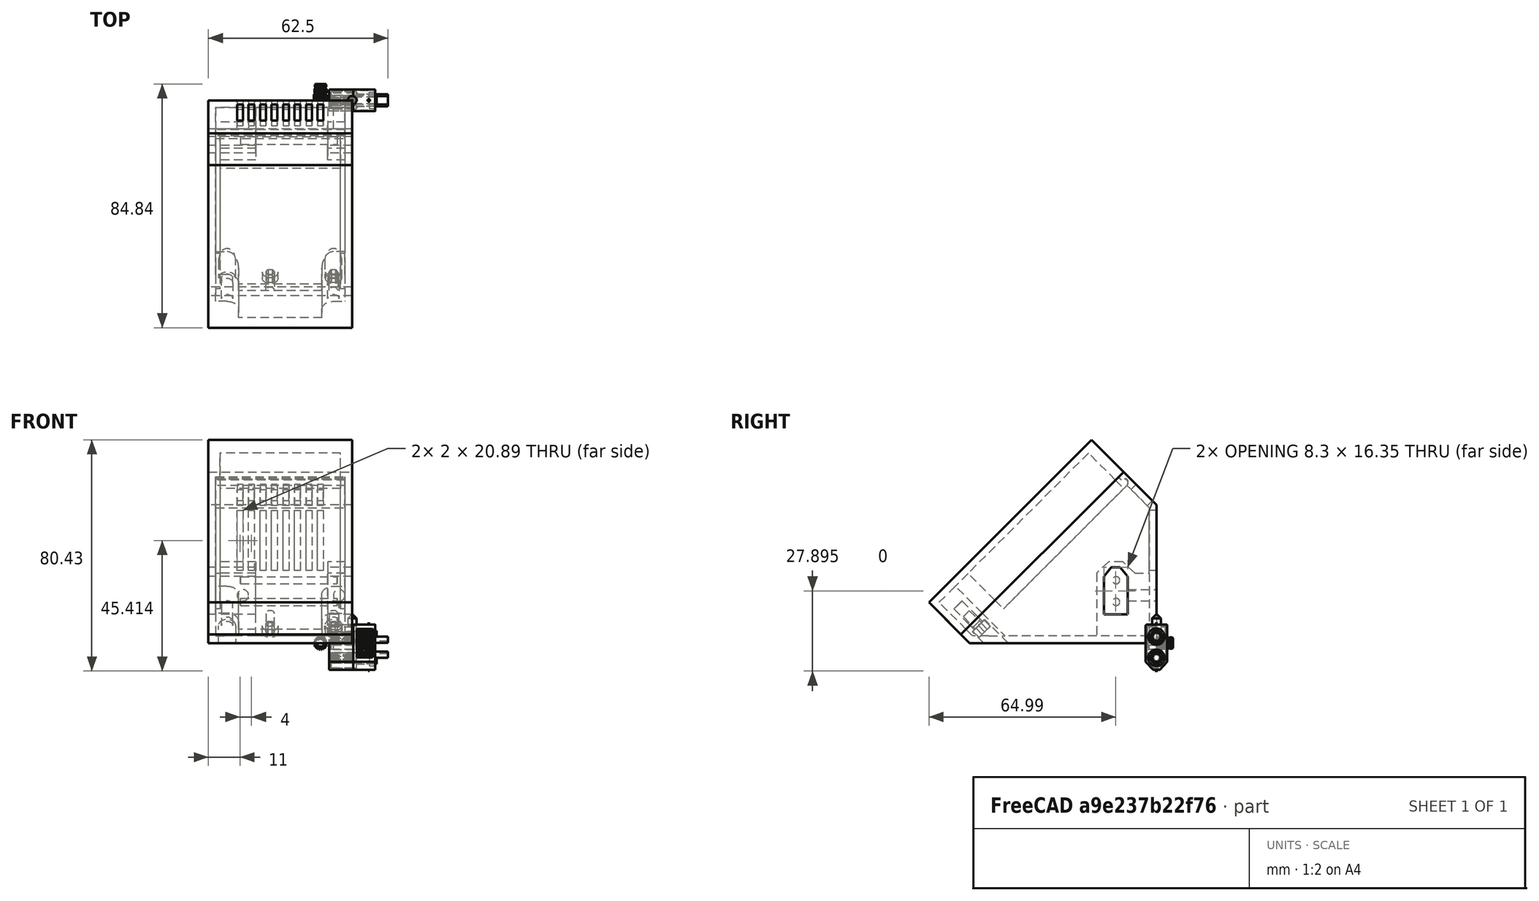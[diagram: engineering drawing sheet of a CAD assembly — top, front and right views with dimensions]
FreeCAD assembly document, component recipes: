
FREECAD ASSEMBLY — COMPONENT RECIPES ("base35mm_009.1")

This assembly document has 8 components, labeled P0..P7 below (a component is one placed body or linked part). 6 of them carry a construction recipe — the FreeCAD feature program that regenerates the part from scratch, quoted from this document or its linked companion documents; the rest are supplied as boundary geometry only. No exploded tour is included for this assembly.
COMPONENT P0 — recipe-attached ("base", modeled in this document).
Construction recipe (the document's own serialized feature program — sketch geometry with constraints, then the solid features built on it; lengths are millimeters unless a unit is written):

FEATURE [PartDesign::FeatureBase] Clone
  BaseFeature = -> Slice_child0
FEATURE [PartDesign::Thickness] Thickness
  Base = -> Clone [Face7]
  BaseFeature = -> Clone
  Intersection = false
  Join = 0
  Mode = 0
  Reversed = true
  SupportTransform = false
  Value = 2.5
  expr: Value = <<sp>>.epaisseurParois
FEATURE [PartDesign::Plane] DatumPlane001  label="planXt"
  AttachmentOffset = pos=(0,0,-2.5) rot=(0,0,1;0rad)
  Length = 110.737
  MapMode = 5
  Placement = pos=(-2.5,6e-16,-6e-16) rot=(0.57735,0.57735,0.57735;2.0944rad)
  ResizeMode = 0
  Support = -> [YZ_Plane002]
  Width = 102.305
  expr: .AttachmentOffset.Base.z = -<<sp>>.epaisseurParois
FEATURE [Sketcher::SketchObject] Sketch002  label="sk_renfortXt"
  FullyConstrained = true
  MapMode = 5
  Placement = pos=(-2.5,6e-16,-6e-16) rot=(0.57735,0.57735,0.57735;2.0944rad)
  Support = -> [DatumPlane001]
  expr: .Constraints.dist = <<sp>>.xt60distanceAngleBord
  expr: .Constraints.epRf = <<sp>>.xt60epRenfort
  expr: Constraints[13] = <<sp>>.xt60largeurFetiere
  expr: Constraints[14] = <<sp>>.xt60hauteur
  expr: Constraints[15] = <<sp>>.xt60hauteurToit
  expr: Constraints[16] = <<sp>>.xt60base
  expr: Constraints[18] = .Constraints.dist
  expr: Constraints[31] = <<sp>>.epaisseurParois
  expr: Constraints[32] = .Constraints.epRf
  expr: Constraints[34] = .Constraints.epRf
  expr: Constraints[45] = <<sp>>.epaisseurParois
  sketch-geometry (17):
    g0: LineSegment StartX=-18.3 StartY=10 StartZ=0 EndX=-18.3 EndY=23.25 EndZ=0
    g1: LineSegment StartX=-18.3 StartY=23.25 StartZ=0 EndX=-15.65 EndY=25.75 EndZ=0
    g2: LineSegment StartX=-15.65 StartY=25.75 StartZ=0 EndX=-12.65 EndY=25.75 EndZ=0
    g3: LineSegment StartX=-12.65 StartY=25.75 StartZ=0 EndX=-10 EndY=23.25 EndZ=0
    g4: LineSegment StartX=-10 StartY=23.25 StartZ=0 EndX=-10 EndY=10 EndZ=0
    g5: LineSegment StartX=-10 StartY=10 StartZ=0 EndX=-18.3 EndY=10 EndZ=0
    g6: LineSegment StartX=-14.15 StartY=10 StartZ=0 EndX=-14.15 EndY=25.75 EndZ=0
    g7: LineSegment StartX=-16.6431 StartY=28.25 StartZ=0 EndX=-20.8 EndY=24.3284 EndZ=0
    g8: LineSegment StartX=-20.8 StartY=24.3284 StartZ=0 EndX=-20.8 EndY=2.5 EndZ=0
    g9: LineSegment StartX=-20.8 StartY=2.5 StartZ=0 EndX=-7.5 EndY=2.5 EndZ=0
    g10: LineSegment StartX=-7.5 StartY=2.5 StartZ=0 EndX=-7.5 EndY=24.3284 EndZ=0
    g11: LineSegment StartX=-7.5 StartY=24.3284 StartZ=0 EndX=-11.6569 EndY=28.25 EndZ=0
    g12: LineSegment StartX=-11.6569 StartY=28.25 StartZ=0 EndX=-16.6431 EndY=28.25 EndZ=0
    g13: LineSegment StartX=-7.5 StartY=24.3284 StartZ=0 EndX=-2.5 EndY=24.3284 EndZ=0
    g14: LineSegment StartX=-2.5 StartY=24.3284 StartZ=0 EndX=-2.5 EndY=2.5 EndZ=0
    g15: LineSegment StartX=-2.5 StartY=2.5 StartZ=0 EndX=-7.5 EndY=2.5 EndZ=0
    g16: LineSegment StartX=-7.5 StartY=2.5 StartZ=0 EndX=-7.5 EndY=24.3284 EndZ=0
  constraints (46):
    c: Vertical(g0)
    c: Coincident(g0,g1)
    c: Coincident(g1,g2)
    c: Horizontal(g2)
    c: Coincident(g2,g3)
    c: Coincident(g3,g4)
    c: Vertical(g4)
    c: Coincident(g4,g5)
    c: Coincident(g5,g0)
    c: Horizontal(g5)
    c: Symmetric(g1,g2,g6)
    c: Equal(g0,g4)
    c: Symmetric(g0,g4,g6)
    c: DistanceX(g2,g2) = 3
    c: DistanceY(g4,g4) = 13.25
    c: DistanceY(g3,g2) = 2.5
    c: DistanceX(g5,g5) = 8.3
    c: DistanceX(g4,g-1) = 10  'dist'
    c: DistanceY(g-1,g4) = 10
    c: Coincident(g7,g8)
    c: Vertical(g8)
    c: Coincident(g8,g9)
    c: Horizontal(g9)
    c: Coincident(g9,g10)
    c: Coincident(g10,g11)
    c: Coincident(g11,g12)
    c: Coincident(g12,g7)
    c: Symmetric(g7,g10,g6)
    c: Symmetric(g7,g11,g6)
    c: Symmetric(g8,g9,g6)
    c: DistanceX(g8,g0) = 2.5  'epRf'
    c: DistanceY(g-1,g9) = 2.5
    c: Distance(g7,g1) = 2.5
    c: Parallel(g1,g7)
    c: DistanceY(g2,g11) = 2.5
    c: Coincident(g13,g14)
    c: Coincident(g14,g15)
    c: Coincident(g15,g16)
    c: Coincident(g16,g13)
    c: Horizontal(g13)
    c: Horizontal(g15)
    c: Vertical(g14)
    c: Vertical(g16)
    c: Coincident(g13,g11)
    c: Horizontal(g14,g9)
    c: DistanceX(g14,g-1) = 2.5
FEATURE [PartDesign::Pad] Pad001  label="renfortXt"
  AllowMultiFace = false
  BaseFeature = -> Thickness
  Direction = (1,-1e-16,1e-16)
  Length = 45
  Length2 = 100
  Profile = -> Sketch002
  Reversed = true
  Type = 0
  expr: Length = <<sp>>.largeurModuleBase - 2 * <<sp>>.epaisseurParois
FEATURE [Sketcher::SketchObject] Sketch003  label="sk_trouXt"
  FullyConstrained = true
  MapMode = 5
  Placement = pos=(0,0,0) rot=(0.57735,0.57735,0.57735;2.0944rad)
  Support = -> [YZ_Plane002]
  expr: .Constraints.dist = <<sp>>.xt60distanceAngleBord
  expr: Constraints[13] = <<sp>>.xt60base
  expr: Constraints[14] = <<sp>>.xt60hauteur
  expr: Constraints[15] = <<sp>>.xt60hauteurToit + <<sp>>.xtJeu
  expr: Constraints[16] = <<sp>>.xt60largeurFetiere
  expr: Constraints[18] = .Constraints.dist
  sketch-geometry (7):
    g0: LineSegment StartX=-18.3 StartY=10 StartZ=0 EndX=-18.3 EndY=23.25 EndZ=0
    g1: LineSegment StartX=-18.3 StartY=23.25 StartZ=0 EndX=-15.65 EndY=26.35 EndZ=0
    g2: LineSegment StartX=-15.65 StartY=26.35 StartZ=0 EndX=-12.65 EndY=26.35 EndZ=0
    g3: LineSegment StartX=-12.65 StartY=26.35 StartZ=0 EndX=-10 EndY=23.25 EndZ=0
    g4: LineSegment StartX=-10 StartY=23.25 StartZ=0 EndX=-10 EndY=10 EndZ=0
    g5: LineSegment StartX=-10 StartY=10 StartZ=0 EndX=-18.3 EndY=10 EndZ=0
    g6: LineSegment StartX=-14.15 StartY=10 StartZ=0 EndX=-14.15 EndY=26.35 EndZ=0
  constraints (19):
    c: Vertical(g0)
    c: Coincident(g0,g1)
    c: Coincident(g1,g2)
    c: Horizontal(g2)
    c: Coincident(g2,g3)
    c: Coincident(g3,g4)
    c: Coincident(g4,g5)
    c: Coincident(g5,g0)
    c: Horizontal(g5)
    c: Symmetric(g1,g2,g6)
    c: Symmetric(g0,g3,g6)
    c: Vertical(g6)
    c: Symmetric(g0,g4,g6)
    c: DistanceX(g5,g5) = 8.3
    c: DistanceY(g4,g4) = 13.25
    c: DistanceY(g3,g2) = 3.1
    c: DistanceX(g2,g2) = 3
    c: DistanceX(g4,g-1) = 10  'dist'
    c: DistanceY(g-1,g4) = 10
FEATURE [PartDesign::Pocket] Pocket
  AllowMultiFace = false
  BaseFeature = -> Pad001
  Direction = (-1,2e-16,-3e-16)
  Length = 50
  Length2 = 100
  Profile = -> Sketch003
  Type = 0
  expr: Length = <<sp>>.largeurModuleBase
FEATURE [PartDesign::Plane] DatumPlane002  label="planDecoupeRenfortXt"
  AttachmentOffset = pos=(0,0,2.5) rot=(0,0,1;0rad)
  Length = 90.9281
  MapMode = 5
  Placement = pos=(0,-2.5,-6e-16) rot=(1,0,0;1.5708rad)
  ResizeMode = 0
  Support = -> [XZ_Plane002]
  Width = 100.497
  expr: .AttachmentOffset.Base.z = <<sp>>.epaisseurParois
FEATURE [Sketcher::SketchObject] Sketch004  label="sk_decoupRenfXt"
  FullyConstrained = true
  MapMode = 5
  Placement = pos=(0,-2.5,-6e-16) rot=(1,0,0;1.5708rad)
  Support = -> [DatumPlane002]
  expr: Constraints[10] = <<sp>>.xt60LongueurRenfortPetit + <<sp>>.epaisseurParois
  expr: Constraints[11] = <<sp>>.largeurModuleBase - (<<sp>>.xt60longueurRenfortGrand + <<sp>>.epaisseurParois)
  expr: Constraints[8] = <<sp>>.epaisseurParois
  expr: Constraints[9] = <<sp>>.xt60distanceAngleBord + <<sp>>.xt60hauteur + <<sp>>.xt60hauteurToit + <<sp>>.xt60epRenfort
  sketch-geometry (4):
    g0: LineSegment StartX=-33.5 StartY=28.25 StartZ=0 EndX=-8.5 EndY=28.25 EndZ=0
    g1: LineSegment StartX=-8.5 StartY=28.25 StartZ=0 EndX=-8.5 EndY=2.5 EndZ=0
    g2: LineSegment StartX=-8.5 StartY=2.5 StartZ=0 EndX=-33.5 EndY=2.5 EndZ=0
    g3: LineSegment StartX=-33.5 StartY=2.5 StartZ=0 EndX=-33.5 EndY=28.25 EndZ=0
  constraints (12):
    c: Coincident(g0,g1)
    c: Coincident(g1,g2)
    c: Coincident(g2,g3)
    c: Coincident(g3,g0)
    c: Horizontal(g0)
    c: Horizontal(g2)
    c: Vertical(g1)
    c: Vertical(g3)
    c: DistanceY(g-1,g1) = 2.5
    c: DistanceY(g-1,g0) = 28.25
    c: DistanceX(g1,g-1) = 8.5
    c: DistanceX(g2,g-1) = 33.5
FEATURE [PartDesign::Pocket] Pocket001  label="decoupeRenfXt"
  AllowMultiFace = false
  BaseFeature = -> Pocket
  Direction = (0,1,2e-16)
  Length = 23.3
  Length2 = 100
  Profile = -> Sketch004
  Reversed = true
  Type = 0
  expr: Length = <<sp>>.xt60distanceAngleBord + <<sp>>.xt60base + 2 * <<sp>>.xt60epRenfort
FEATURE [Sketcher::SketchObject] Sketch005  label="xt60PercagePostMale"
  FullyConstrained = true
  MapMode = 5
  Placement = pos=(0,0,0) rot=(1,0,0;1.5708rad)
  Support = -> [XZ_Plane002]
  expr: Constraints[0] = <<sp>>.insertDiamPercage
  expr: Constraints[1] = <<sp>>.insertDistanceTrouBordMale
  expr: Constraints[2] = <<sp>>.insertHauteur
  sketch-geometry (1):
    g0: Circle CenterX=-4.5 CenterY=16.625 CenterZ=0 NormalX=0 NormalY=0 NormalZ=1 AngleXU=0 Radius=2
  constraints (3):
    c: Diameter(g0) = 4
    c: DistanceX(g0,g-1) = 4.5
    c: DistanceY(g-1,g0) = 16.625
FEATURE [PartDesign::Pocket] Pocket002  label="insertXtMale"
  AllowMultiFace = false
  BaseFeature = -> Pocket001
  Direction = (0,1,2e-16)
  Length = 10
  Length2 = 100
  Profile = -> Sketch005
  Reversed = true
  Type = 0
  expr: Length = <<sp>>.insertProfondeurPercage
FEATURE [Sketcher::SketchObject] Sketch006  label="xt60PercagePostFem"
  FullyConstrained = true
  MapMode = 5
  Placement = pos=(0,0,0) rot=(1,0,0;1.5708rad)
  Support = -> [XZ_Plane002]
  expr: Constraints[0] = <<sp>>.insertDiamPercage
  expr: Constraints[1] = <<sp>>.insertDistanceTrouBordFem
  expr: Constraints[2] = <<sp>>.insertHauteur
  sketch-geometry (1):
    g0: Circle CenterX=-38 CenterY=16.625 CenterZ=0 NormalX=0 NormalY=0 NormalZ=1 AngleXU=0 Radius=2
  constraints (3):
    c: Diameter(g0) = 4
    c: DistanceX(g0,g-1) = 38
    c: DistanceY(g-1,g0) = 16.625
FEATURE [PartDesign::Pocket] Pocket003  label="insertXt60Fem"
  AllowMultiFace = false
  BaseFeature = -> Pocket002
  Direction = (0,1,2e-16)
  Length = 10
  Length2 = 100
  Profile = -> Sketch006
  Reversed = true
  Type = 0
  expr: Length = <<sp>>.insertProfondeurPercage
FEATURE [PartDesign::Plane] DatumPlane003
  AttachmentOffset = pos=(0,0,2.5) rot=(0,0,1;0rad)
  Length = 91.7033
  MapMode = 2
  Placement = pos=(0,0,2.5) rot=(0,0,1;0rad)
  ResizeMode = 0
  Support = -> [XY_Plane002]
  Width = 109.703
  expr: .AttachmentOffset.Base.z = <<sp>>.epaisseurParois
FEATURE [PartDesign::Plane] DatumPlane004  label="planTrancheur"
  AttachmentOffset = pos=(0,0,71) rot=(-1,0,0;0.785398rad)
  Length = 94.4082
  MapMode = 5
  Placement = pos=(0,-71,-1.58e-14) rot=(1,0,0;0.785398rad)
  ResizeMode = 0
  Support = -> [XZ_Plane002]
  Width = 144.968
  expr: .AttachmentOffset.Base.z = <<sp>>.planTrancheur
FEATURE [Sketcher::SketchObject] Sketch008
  FullyConstrained = true
  MapMode = 5
  Placement = pos=(0,-71,-2.13e-14) rot=(1,0,0;0.785398rad)
  Support = -> [DatumPlane004]
  expr: .Constraints.dist = <<sp>>.epaisseurParois
  expr: Constraints[13] = <<sp>>.epaisseurParois
  expr: Constraints[16] = <<sp>>.insertDiamPercage / 2 + <<sp>>.insertFAVMargeDist
  expr: Constraints[1] = <<sp>>.insertFavDistAuZeroDuPLan
  expr: Constraints[21] = <<sp>>.insertFAVDistBord
  expr: Constraints[22] = <<sp>>.largeurModuleBase - <<sp>>.epaisseurParois
  sketch-geometry (7):
    g0: LineSegment StartX=-2.5 StartY=4.24264 StartZ=0 EndX=-47.5 EndY=4.24264 EndZ=0
    g1: LineSegment StartX=-6.5 StartY=14.7426 StartZ=0 EndX=-2.5 EndY=14.7426 EndZ=0
    g2: LineSegment StartX=-2.5 StartY=14.7426 StartZ=0 EndX=-2.5 EndY=6.74264 EndZ=0
    g3: LineSegment StartX=-2.5 StartY=6.74264 StartZ=0 EndX=-10.5 EndY=6.74264 EndZ=0
    g4: LineSegment StartX=-10.5 StartY=6.74264 StartZ=0 EndX=-10.5 EndY=10.7426 EndZ=0
    g5: ArcOfCircle CenterX=-6.5 CenterY=10.7426 CenterZ=0 NormalX=0 NormalY=0 NormalZ=1 AngleXU=0 Radius=4 StartAngle=1.5708 EndAngle=3.14159
    g6: LineSegment StartX=-6.5 StartY=10.7426 StartZ=0 EndX=-6.5 EndY=6.74264 EndZ=0
  constraints (23):
    c: Horizontal(g0)
    c: DistanceY(g-1,g0) = 4.24264
    c: DistanceX(g0,g-1) = 2.5  'dist'
    c: Horizontal(g1)
    c: Coincident(g1,g2)
    c: Vertical(g2)
    c: Coincident(g2,g3)
    c: Horizontal(g3)
    c: Coincident(g3,g4)
    c: Vertical(g4)
    c: Vertical(g2,g0)
    c: Equal(g3,g2)
    c: Equal(g4,g1)
    c: DistanceY(g0,g2) = 2.5
    c: Coincident(g5,g4)
    c: Coincident(g5,g1)
    c: DistanceX(g5,g2) = 4
    c: Coincident(g6,g5)
    c: PointOnObject(g6,g3)
    c: Vertical(g6)
    c: Vertical(g5,g1)
    c: DistanceX(g3,g3) = 8
    c: DistanceX(g0,g-1) = 47.5
FEATURE [PartDesign::Pad] Pad003  label="padTrouFAVDroite"
  AllowMultiFace = false
  BaseFeature = -> Pocket003
  Direction = (0,-0.707107,0.707107)
  Length = 10
  Length2 = 100
  Profile = -> Sketch008
  Reversed = true
  Type = 3
  UpToFace = -> DatumPlane003
FEATURE [Sketcher::SketchObject] Sketch009
  FullyConstrained = true
  MapMode = 5
  Placement = pos=(0,-71,-2.13e-14) rot=(1,0,0;0.785398rad)
  Support = -> [DatumPlane004]
  expr: .Constraints.larg = <<sp>>.insertFAVDistBord
  expr: Constraints[11] = .Constraints.larg / 2
  expr: Constraints[12] = <<sp>>.largeurModuleBase
  expr: Constraints[13] = <<sp>>.insertFavDistAuZeroDuPLan
  expr: Constraints[14] = <<sp>>.epaisseurParois
  expr: Constraints[15] = <<sp>>.epaisseurParois
  expr: Constraints[8] = .Constraints.larg
  sketch-geometry (6):
    g0: LineSegment StartX=-47.5 StartY=6.74264 StartZ=0 EndX=-39.5 EndY=6.74264 EndZ=0
    g1: LineSegment StartX=-39.5 StartY=6.74264 StartZ=0 EndX=-39.5 EndY=10.7426 EndZ=0
    g2: LineSegment StartX=-43.5 StartY=14.7426 StartZ=0 EndX=-47.5 EndY=14.7426 EndZ=0
    g3: LineSegment StartX=-47.5 StartY=14.7426 StartZ=0 EndX=-47.5 EndY=6.74264 EndZ=0
    g4: ArcOfCircle CenterX=-43.5 CenterY=10.7426 CenterZ=0 NormalX=0 NormalY=0 NormalZ=1 AngleXU=0 Radius=4 StartAngle=0 EndAngle=1.5708
    g5: GeomPoint X=-50 Y=4.24264 Z=0
  constraints (16):
    c: Coincident(g0,g1)
    c: Coincident(g2,g3)
    c: Coincident(g3,g0)
    c: Horizontal(g0)
    c: Horizontal(g2)
    c: Vertical(g1)
    c: Vertical(g3)
    c: DistanceX(g0,g0) = 8  'larg'
    c: DistanceY(g3,g3) = 8
    c: Tangent(g2,g4) = -1.5708
    c: Tangent(g1,g4) = -1.5708
    c: DistanceX(g0,g4) = 4
    c: DistanceX(g5,g-1) = 50
    c: DistanceY(g-1,g5) = 4.24264
    c: DistanceX(g5,g0) = 2.5
    c: DistanceY(g5,g0) = 2.5
FEATURE [PartDesign::Pad] Pad004  label="padTrouFavGauche"
  AllowMultiFace = false
  BaseFeature = -> Pad003
  Direction = (0,-0.707107,0.707107)
  Length = 10
  Length2 = 100
  Profile = -> Sketch009
  Type = 3
  UpToFace = -> DatumPlane003 [Plane]
FEATURE [Sketcher::SketchObject] Sketch010
  FullyConstrained = true
  MapMode = 5
  Placement = pos=(0,-71,-2.13e-14) rot=(1,0,0;0.785398rad)
  Support = -> [DatumPlane004]
  expr: Constraints[0] = <<sp>>.insertFAVDistBord / 2 + <<sp>>.epaisseurParois
  expr: Constraints[1] = <<sp>>.insertFavDistAuZeroDuPLan + <<sp>>.epaisseurParois + <<sp>>.insertFAVDistBord / 2
  expr: Constraints[2] = <<sp>>.insertDiamPercage
  sketch-geometry (1):
    g0: Circle CenterX=-6.5 CenterY=10.7426 CenterZ=0 NormalX=0 NormalY=0 NormalZ=1 AngleXU=0 Radius=2
  constraints (3):
    c: DistanceX(g0,g-1) = 6.5
    c: DistanceY(g-1,g0) = 10.7426
    c: Diameter(g0) = 4
FEATURE [PartDesign::Pocket] Pocket004  label="trouDroit"
  AllowMultiFace = false
  BaseFeature = -> Pad004
  Direction = (0,0.707107,-0.707107)
  Length = 5
  Length2 = 100
  Profile = -> Sketch010
  Type = 1
FEATURE [Sketcher::SketchObject] Sketch011
  FullyConstrained = true
  MapMode = 5
  Placement = pos=(0,-71,-2.13e-14) rot=(1,0,0;0.785398rad)
  Support = -> [DatumPlane004]
  expr: Constraints[0] = <<sp>>.insertDiamPercage
  expr: Constraints[1] = <<sp>>.largeurModuleBase - <<sp>>.epaisseurParois - <<sp>>.insertFAVDistBord / 2
  expr: Constraints[2] = <<sp>>.insertFavDistAuZeroDuPLan + <<sp>>.epaisseurParois + <<sp>>.insertFAVDistBord / 2
  sketch-geometry (1):
    g0: Circle CenterX=-43.5 CenterY=10.7426 CenterZ=0 NormalX=0 NormalY=0 NormalZ=1 AngleXU=0 Radius=2
  constraints (3):
    c: Diameter(g0) = 4
    c: DistanceX(g0,g-1) = 43.5
    c: DistanceY(g-1,g0) = 10.7426
FEATURE [PartDesign::Pocket] Pocket005  label="trouGauche"
  AllowMultiFace = false
  BaseFeature = -> Pocket004
  Direction = (0,0.707107,-0.707107)
  Length = 5
  Length2 = 100
  Profile = -> Sketch011
  Type = 1
FEATURE [PartDesign::Plane] DatumPlane005  label="planTeteVisFav"
  AttachmentOffset = pos=(0,0,68) rot=(-1,0,0;0.785398rad)
  Length = 94.4082
  MapMode = 5
  Placement = pos=(0,-68,-1.51e-14) rot=(1,0,0;0.785398rad)
  ResizeMode = 0
  Support = -> [XZ_Plane002]
  Width = 144.968
  expr: .AttachmentOffset.Base.z = <<sp>>.planTrancheur - 3
FEATURE [Sketcher::SketchObject] Sketch012
  ExternalGeometry = -> [Pocket005]
  FullyConstrained = true
  MapMode = 5
  Placement = pos=(0,-68,-1.42e-14) rot=(1,0,0;0.785398rad)
  Support = -> [DatumPlane005]
  expr: Constraints[1] = <<sp>>.visM3DiamEncastrement
  sketch-geometry (2):
    g0: Circle CenterX=-6.5 CenterY=8.62132 CenterZ=0 NormalX=0 NormalY=0 NormalZ=1 AngleXU=0 Radius=3
    g1: Circle CenterX=-43.5 CenterY=8.62132 CenterZ=0 NormalX=0 NormalY=0 NormalZ=1 AngleXU=0 Radius=3
  constraints (4):
    c: Equal(g0,g1)
    c: Diameter(g1) = 6
    c: Coincident(g1,g-4)
    c: Coincident(g-3,g0)
FEATURE [PartDesign::Pocket] Pocket006  label="evidementTeteVisFav"
  AllowMultiFace = false
  BaseFeature = -> Pocket005
  Direction = (0,0.707107,-0.707107)
  Length = 20
  Length2 = 100
  Profile = -> Sketch012
  Type = 1
FEATURE [Sketcher::SketchObject] Sketch014
  FullyConstrained = true
  MapMode = 5
  Placement = pos=(0,0,0) rot=(1,0,0;1.5708rad)
  Support = -> [XZ_Plane002]
  expr: Constraints[12] = <<sp>>.xt60distanceAngleBord + <<sp>>.xt60hauteur + <<sp>>.ventilDistBordFente
  expr: Constraints[13] = <<sp>>.ventilLargeurFentes
  expr: Constraints[14] = <<sp>>.ventilEcartfente / 2
  expr: Constraints[15] = <<sp>>.hauteurDuDos - <<sp>>.ventilDistBordFente
  expr: Constraints[2] = <<sp>>.hauteurDuDos
  expr: Constraints[3] = <<sp>>.largeurModuleBase / 2
  sketch-geometry (5):
    g0: LineSegment StartX=-25 StartY=0 StartZ=0 EndX=-25 EndY=48.1371 EndZ=0
    g1: LineSegment StartX=-28 StartY=46.1371 StartZ=0 EndX=-26 EndY=46.1371 EndZ=0
    g2: LineSegment StartX=-26 StartY=46.1371 StartZ=0 EndX=-26 EndY=25.25 EndZ=0
    g3: LineSegment StartX=-26 StartY=25.25 StartZ=0 EndX=-28 EndY=25.25 EndZ=0
    g4: LineSegment StartX=-28 StartY=25.25 StartZ=0 EndX=-28 EndY=46.1371 EndZ=0
  constraints (16):
    c: PointOnObject(g0,g-1)
    c: Vertical(g0)
    c: DistanceY(g0,g0) = 48.1371
    c: DistanceX(g0,g-1) = 25
    c: Coincident(g1,g2)
    c: Coincident(g2,g3)
    c: Coincident(g3,g4)
    c: Coincident(g4,g1)
    c: Horizontal(g1)
    c: Horizontal(g3)
    c: Vertical(g2)
    c: Vertical(g4)
    c: DistanceY(g-1,g2) = 25.25
    c: DistanceX(g1,g1) = 2
    c: DistanceX(g2,g0) = 1
    c: DistanceY(g-1,g1) = 46.1371
FEATURE [PartDesign::Pocket] Pocket008  label="ventilFente1"
  AllowMultiFace = false
  BaseFeature = -> Pocket006
  Direction = (0,1,2e-16)
  Length = 2.5
  Length2 = 100
  Profile = -> Sketch014
  Reversed = true
  Type = 0
  expr: Length = <<sp>>.epaisseurParois
FEATURE [PartDesign::LinearPattern] LinearPattern  label="ventilDosRepeat1"
  BaseFeature = -> Pocket008
  Direction = -> Sketch014 [H_Axis]
  Length = 12
  Occurrences = 4
  Originals = -> [Pocket008]
  Reversed = true
  expr: Length = <<sp>>.ventilLargeurRepet
  expr: Occurrences = <<sp>>.ventilNbrFents
FEATURE [PartDesign::LinearPattern] LinearPattern001  label="ventilDosRepeat2"
  BaseFeature = -> LinearPattern
  Direction = -> Sketch014 [H_Axis]
  Length = 16
  Occurrences = 5
  Originals = -> [Pocket008]
  expr: Length = <<sp>>.ventilLargeurRepet + <<sp>>.ventilEcartfente + <<sp>>.ventilLargeurFentes
  expr: Occurrences = <<sp>>.ventilNbrFents + 1
FEATURE [PartDesign::Plane] DatumPlane006  label="planVentilSup"
  AttachmentOffset = pos=(0,0,-48.1371) rot=(1,0,0;0.785398rad)
  Length = 94.4082
  MapMode = 5
  Placement = pos=(0,48.1371,1.07e-14) rot=(1,0,0;2.35619rad)
  ResizeMode = 0
  Support = -> [XZ_Plane002]
  Width = 144.968
  expr: .AttachmentOffset.Base.z = -<<sp>>.hauteurDuDos
FEATURE [Sketcher::SketchObject] Sketch015
  FullyConstrained = true
  MapMode = 5
  Placement = pos=(0,48.1371,1.07e-14) rot=(1,0,0;2.35619rad)
  Support = -> [DatumPlane006]
  expr: Constraints[10] = <<sp>>.ventilLargeurFentes
  expr: Constraints[11] = (<<sp>>.largeurModuleBase + <<sp>>.ventilEcartfente) / 2
  expr: Constraints[8] = <<sp>>.distanceAuZeroPlanBorArriere + <<sp>>.ventilDistBordFente
  expr: Constraints[9] = <<sp>>.longPetitRetSupSansFav - 2 * <<sp>>.ventilDistBordFente - <<sp>>.favBordureProf
  sketch-geometry (4):
    g0: LineSegment StartX=-26 StartY=78.0926 StartZ=0 EndX=-28 EndY=78.0926 EndZ=0
    g1: LineSegment StartX=-28 StartY=78.0926 StartZ=0 EndX=-28 EndY=70.0761 EndZ=0
    g2: LineSegment StartX=-28 StartY=70.0761 StartZ=0 EndX=-26 EndY=70.0761 EndZ=0
    g3: LineSegment StartX=-26 StartY=70.0761 StartZ=0 EndX=-26 EndY=78.0926 EndZ=0
  constraints (12):
    c: Coincident(g0,g1)
    c: Coincident(g1,g2)
    c: Coincident(g2,g3)
    c: Coincident(g3,g0)
    c: Horizontal(g0)
    c: Horizontal(g2)
    c: Vertical(g1)
    c: Vertical(g3)
    c: DistanceY(g-1,g2) = 70.0761
    c: DistanceY(g2,g0) = 8.01652
    c: DistanceX(g0,g0) = 2
    c: DistanceX(g2,g-1) = 26
FEATURE [PartDesign::Pocket] Pocket009  label="ventilSupFente"
  AllowMultiFace = false
  BaseFeature = -> LinearPattern001
  Direction = (0,0.707107,0.707107)
  Length = 5
  Length2 = 100
  Profile = -> Sketch015
  Reversed = true
  Type = 0
FEATURE [PartDesign::LinearPattern] LinearPattern002  label="ventilSupRepeat1"
  BaseFeature = -> Pocket009
  Direction = -> Sketch015 [H_Axis]
  Length = 12
  Occurrences = 4
  Originals = -> [Pocket009]
  Reversed = true
  expr: Length = <<sp>>.ventilLargeurRepet
  expr: Occurrences = <<sp>>.ventilNbrFents
FEATURE [PartDesign::LinearPattern] LinearPattern003  label="ventilSupRepeat2"
  BaseFeature = -> LinearPattern002
  Direction = -> Sketch015 [H_Axis]
  Length = 16
  Occurrences = 5
  Originals = -> [Pocket009]
  expr: Length = <<sp>>.ventilLargeurRepet + <<sp>>.ventilEcartfente + <<sp>>.ventilLargeurFentes
  expr: Occurrences = <<sp>>.ventilNbrFents + 1
FEATURE [PartDesign::Body] Body001  label="base"
  BaseFeature = -> Slice_child0
  Group = -> [Clone,Thickness,DatumPlane001,Sketch002,Pad001,Sketch003,Pocket,DatumPlane002,Sketch004,Pocket001,Sketch005,Pocket002,Sketch006,Pocket003,DatumPlane003,DatumPlane004,Sketch008,Pad003,Sketch009,Pad004,Sketch010,Pocket004,Sketch011,Pocket005,DatumPlane005,Sketch012,Pocket006,Sketch014,Pocket008,LinearPattern,LinearPattern001,DatumPlane006,Sketch015,Pocket009,LinearPattern002,LinearPattern003,+3 more]
  Origin = -> Origin002
  Tip = -> Pocket015
COMPONENT P1 — recipe-attached ("faceAvant", modeled in this document).
Construction recipe (the document's own serialized feature program — sketch geometry with constraints, then the solid features built on it; lengths are millimeters unless a unit is written):

FEATURE [PartDesign::FeatureBase] Clone001
  BaseFeature = -> Slice_child1
FEATURE [PartDesign::Thickness] Thickness001
  Base = -> Clone001 [Face5]
  BaseFeature = -> Clone001
  Intersection = false
  Join = 0
  Mode = 0
  Reversed = true
  SupportTransform = false
  Value = 2.5
  expr: Value = <<sp>>.epaisseurParois
FEATURE [PartDesign::Plane] DatumPlane007  label="planTrancheurBis"
  AttachmentOffset = pos=(0,0,71) rot=(-1,0,0;0.785398rad)
  Length = 95.5901
  MapMode = 5
  Placement = pos=(0,-71,-1.58e-14) rot=(1,0,0;0.785398rad)
  ResizeMode = 0
  Support = -> [XZ_Plane003]
  Width = 161.907
  expr: .AttachmentOffset.Base.z = <<sp>>.planTrancheur
FEATURE [Sketcher::SketchObject] Sketch016  label="sk_insertFavDroit"
  FullyConstrained = true
  MapMode = 5
  Placement = pos=(0,-71,-2.13e-14) rot=(1,0,0;0.785398rad)
  Support = -> [DatumPlane007]
  expr: Constraints[11] = <<sp>>.insertFAVDistBord
  expr: Constraints[14] = <<sp>>.insertFAVDistBord / 2
  expr: Constraints[7] = <<sp>>.epaisseurParois
  expr: Constraints[8] = <<sp>>.insertFavDistAuZeroDuPLan + <<sp>>.epaisseurParois
  expr: Constraints[9] = <<sp>>.insertFAVDistBord
  sketch-geometry (5):
    g0: LineSegment StartX=-6.5 StartY=14.7426 StartZ=0 EndX=-2.5 EndY=14.7426 EndZ=0
    g1: LineSegment StartX=-2.5 StartY=14.7426 StartZ=0 EndX=-2.5 EndY=6.74264 EndZ=0
    g2: LineSegment StartX=-2.5 StartY=6.74264 StartZ=0 EndX=-10.5 EndY=6.74264 EndZ=0
    g3: LineSegment StartX=-10.5 StartY=6.74264 StartZ=0 EndX=-10.5 EndY=10.7426 EndZ=0
    g4: ArcOfCircle CenterX=-6.5 CenterY=10.7426 CenterZ=0 NormalX=0 NormalY=0 NormalZ=1 AngleXU=0 Radius=4 StartAngle=1.5708 EndAngle=3.14159
  constraints (15):
    c: Horizontal(g0)
    c: Coincident(g0,g1)
    c: Vertical(g1)
    c: Coincident(g1,g2)
    c: Horizontal(g2)
    c: Coincident(g2,g3)
    c: Vertical(g3)
    c: DistanceX(g1,g-1) = 2.5
    c: DistanceY(g-1,g1) = 6.74264
    c: DistanceY(g1,g1) = 8
    c: Equal(g3,g0)
    c: DistanceX(g2,g2) = 8
    c: Coincident(g4,g0)
    c: Tangent(g4,g3) = 1.5708
    c: DistanceX(g4,g1) = 4
FEATURE [PartDesign::Pad] Pad005  label="padInsertFavDroit"
  AllowMultiFace = false
  BaseFeature = -> Thickness001
  Direction = (0,-0.707107,0.707107)
  Length = 10
  Length2 = 100
  Profile = -> Sketch016
  Type = 2
FEATURE [Sketcher::SketchObject] Sketch017  label="sp_padInserFavGauch"
  FullyConstrained = true
  MapMode = 5
  Placement = pos=(0,-71,-2.13e-14) rot=(1,0,0;0.785398rad)
  Support = -> [DatumPlane007]
  expr: Constraints[10] = <<sp>>.insertFAVDistBord
  expr: Constraints[12] = <<sp>>.insertFAVDistBord / 2
  expr: Constraints[13] = <<sp>>.largeurModuleBase
  expr: Constraints[14] = <<sp>>.insertFavDistAuZeroDuPLan
  expr: Constraints[15] = <<sp>>.epaisseurParois
  expr: Constraints[16] = <<sp>>.epaisseurParois
  sketch-geometry (6):
    g0: LineSegment StartX=-43.5 StartY=14.7426 StartZ=0 EndX=-47.5 EndY=14.7426 EndZ=0
    g1: LineSegment StartX=-47.5 StartY=14.7426 StartZ=0 EndX=-47.5 EndY=6.74264 EndZ=0
    g2: LineSegment StartX=-47.5 StartY=6.74264 StartZ=0 EndX=-39.5 EndY=6.74264 EndZ=0
    g3: LineSegment StartX=-39.5 StartY=6.74264 StartZ=0 EndX=-39.5 EndY=10.7426 EndZ=0
    g4: ArcOfCircle CenterX=-43.5 CenterY=10.7426 CenterZ=0 NormalX=0 NormalY=0 NormalZ=1 AngleXU=0 Radius=4 StartAngle=0 EndAngle=1.5708
    g5: GeomPoint X=-50 Y=4.24264 Z=0
  constraints (17):
    c: Horizontal(g0)
    c: Coincident(g0,g1)
    c: Vertical(g1)
    c: Coincident(g1,g2)
    c: Horizontal(g2)
    c: Coincident(g2,g3)
    c: Vertical(g3)
    c: Equal(g3,g0)
    c: Equal(g2,g1)
    c: Coincident(g0,g4)
    c: DistanceX(g2,g2) = 8
    c: Tangent(g4,g3) = -1.5708
    c: DistanceX(g0,g0) = 4
    c: DistanceX(g5,g-1) = 50
    c: DistanceY(g-1,g5) = 4.24264
    c: DistanceY(g5,g1) = 2.5
    c: DistanceX(g5,g1) = 2.5
FEATURE [PartDesign::Pad] Pad006  label="padInsertFavGauch"
  AllowMultiFace = false
  BaseFeature = -> Pad005
  Direction = (0,-0.707107,0.707107)
  Length = 10
  Length2 = 100
  Profile = -> Sketch017
  Type = 2
FEATURE [Sketcher::SketchObject] Sketch018  label="skPercageInsertFavDroit"
  FullyConstrained = true
  MapMode = 5
  Placement = pos=(0,-71,-2.13e-14) rot=(1,0,0;0.785398rad)
  Support = -> [DatumPlane007]
  expr: Constraints[0] = <<sp>>.insertDiamPercage
  expr: Constraints[1] = <<sp>>.insertFavDistAuZeroDuPLan + <<sp>>.epaisseurParois + <<sp>>.insertFAVDistBord / 2
  expr: Constraints[2] = <<sp>>.epaisseurParois + <<sp>>.insertFAVDistBord / 2
  expr: Constraints[7] = <<sp>>.largeurModuleBase - 2 * <<sp>>.epaisseurParois - <<sp>>.insertFAVDistBord
  sketch-geometry (3):
    g0: Circle CenterX=-6.5 CenterY=10.7426 CenterZ=0 NormalX=0 NormalY=0 NormalZ=1 AngleXU=0 Radius=2
    g1: Circle CenterX=-43.5 CenterY=10.7426 CenterZ=0 NormalX=0 NormalY=0 NormalZ=1 AngleXU=0 Radius=2
    g2: LineSegment StartX=-43.5 StartY=10.7426 StartZ=0 EndX=-6.5 EndY=10.7426 EndZ=0
  constraints (8):
    c: Diameter(g0) = 4
    c: DistanceY(g-1,g0) = 10.7426
    c: DistanceX(g0,g-1) = 6.5
    c: Equal(g0,g1)
    c: Coincident(g2,g1)
    c: Coincident(g2,g0)
    c: Horizontal(g2)
    c: DistanceX(g2,g2) = 37
FEATURE [PartDesign::Pocket] Pocket010  label="trouInsertFavDroit"
  AllowMultiFace = false
  BaseFeature = -> Pad006
  Direction = (0,0.707107,-0.707107)
  Length = 8
  Length2 = 100
  Profile = -> Sketch018
  Reversed = true
  Type = 0
  expr: Length = <<sp>>.insertFavProfondeur
FEATURE [PartDesign::Plane] DatumPlane011  label="planFaceAvant"
  AttachmentOffset = pos=(0,0,93.2843) rot=(-1,0,0;0.785398rad)
  Length = 95.5901
  MapMode = 5
  Placement = pos=(0,-93.2843,-2.07e-14) rot=(1,0,0;0.785398rad)
  ResizeMode = 0
  Support = -> [XZ_Plane003]
  Width = 161.907
  expr: .AttachmentOffset.Base.z = <<sp>>.planFaceAvant
FEATURE [Sketcher::SketchObject] Sketch030  label="sk_rebordFav"
  FullyConstrained = true
  MapMode = 5
  Placement = pos=(0,-71,-2.13e-14) rot=(1,0,0;0.785398rad)
  Support = -> [DatumPlane007]
  expr: Constraints[0] = <<sp>>.insertFavDistAuZeroDuPLan
  expr: Constraints[19] = <<sp>>.epaisseurParois
  expr: Constraints[20] = <<sp>>.favEpBordure
  expr: Constraints[21] = <<sp>>.favDistBordPlan
  expr: Constraints[22] = <<sp>>.largeurModuleBase - 2 * <<sp>>.epaisseurParois
  expr: Constraints[23] = <<sp>>.favEpBordure
  expr: Constraints[24] = <<sp>>.Face - <<sp>>.epaisseurParois
  expr: Constraints[25] = <<sp>>.favEpBordure
  sketch-geometry (9):
    g0: GeomPoint X=0 Y=4.24264 Z=0
    g1: LineSegment StartX=-47.5 StartY=20.9853 StartZ=0 EndX=-47.5 EndY=81.7426 EndZ=0
    g2: LineSegment StartX=-47.5 StartY=81.7426 StartZ=0 EndX=-2.5 EndY=81.7426 EndZ=0
    g3: LineSegment StartX=-2.5 StartY=81.7426 StartZ=0 EndX=-2.5 EndY=20.9853 EndZ=0
    g4: LineSegment StartX=-2.5 StartY=20.9853 StartZ=0 EndX=-4 EndY=20.9853 EndZ=0
    g5: LineSegment StartX=-4 StartY=20.9853 StartZ=0 EndX=-4 EndY=80.2426 EndZ=0
    g6: LineSegment StartX=-4 StartY=80.2426 StartZ=0 EndX=-46 EndY=80.2426 EndZ=0
    g7: LineSegment StartX=-46 StartY=80.2426 StartZ=0 EndX=-46 EndY=20.9853 EndZ=0
    g8: LineSegment StartX=-46 StartY=20.9853 StartZ=0 EndX=-47.5 EndY=20.9853 EndZ=0
  constraints (26):
    c: DistanceY(g-1,g0) = 4.24264
    c: Vertical(g0,g-1)
    c: Vertical(g1)
    c: Coincident(g1,g2)
    c: Horizontal(g2)
    c: Coincident(g2,g3)
    c: Vertical(g3)
    c: Coincident(g3,g4)
    c: Horizontal(g4)
    c: Coincident(g4,g5)
    c: Vertical(g5)
    c: Coincident(g5,g6)
    c: Horizontal(g6)
    c: Coincident(g6,g7)
    c: Vertical(g7)
    c: Coincident(g7,g8)
    c: Coincident(g8,g1)
    c: Horizontal(g8)
    c: Horizontal(g7,g4)
    c: DistanceX(g3,g0) = 2.5
    c: DistanceX(g4,g4) = 1.5
    c: DistanceY(g0,g3) = 16.7426
    c: DistanceX(g1,g3) = 45
    c: DistanceY(g5,g2) = 1.5
    c: DistanceY(g0,g2) = 77.5
    c: DistanceX(g1,g7) = 1.5
FEATURE [PartDesign::Pad] Pad014  label="favRebordSupport"
  AllowMultiFace = false
  BaseFeature = -> Pocket010
  Direction = (0,-0.707107,0.707107)
  Length = 10
  Length2 = 100
  Profile = -> Sketch030
  Type = 3
  UpToFace = -> Pocket010 [Face13]
FEATURE [PartDesign::Pad] Pad015  label="favRebord"
  AllowMultiFace = false
  BaseFeature = -> Pad014
  Direction = (0,-0.707107,0.707107)
  Length = 4.15
  Length2 = 100
  Profile = -> Sketch030
  Reversed = true
  Type = 0
  expr: Length = <<sp>>.favBordureProf
FEATURE [Sketcher::SketchObject] Sketch031  label="sk_bourlet"
  ExternalGeometry = -> [Pad015]
  FullyConstrained = true
  MapMode = 5
  Placement = pos=(-2.5,0,0) rot=(0.57735,0.57735,0.57735;2.0944rad)
  Support = -> [Pad015]
  expr: Constraints[3] = <<sp>>.bourletMaintientRayon - <<sp>>.bourletRayonJeu
  sketch-geometry (2):
    g0: ArcOfCircle CenterX=-11.184 CenterY=55.7855 CenterZ=0 NormalX=0 NormalY=0 NormalZ=1 AngleXU=0 Radius=1.3 StartAngle=5.49779 EndAngle=8.63938
    g1: LineSegment StartX=-12.1032 StartY=56.7048 StartZ=0 EndX=-10.2647 EndY=54.8663 EndZ=0
  constraints (6):
    c: Coincident(g0,g-3)
    c: PointOnObject(g0,g-3)
    c: PointOnObject(g0,g-3)
    c: Radius(g0) = 1.3
    c: Coincident(g1,g0)
    c: Coincident(g1,g0)
FEATURE [PartDesign::Pad] Pad016  label="bourlet"
  AllowMultiFace = false
  BaseFeature = -> Pad015
  Direction = (1,0,0)
  Length = 10
  Length2 = 100
  Profile = -> Sketch031
  Reversed = true
  Type = 3
  UpToFace = -> Pad015 [Face11]
FEATURE [PartDesign::Body] Body002  label="faceAvant"
  BaseFeature = -> Slice_child1
  Group = -> [Clone001,Thickness001,DatumPlane007,Sketch016,Pad005,Sketch017,Pad006,Sketch018,Pocket010,DatumPlane011,Sketch030,Pad014,Pad015,Sketch031,Pad016]
  Origin = -> Origin003
  Tip = -> Pad016
COMPONENT P2 — recipe-attached ("Link", modeled in this document).
Construction recipe (the document's own serialized feature program — sketch geometry with constraints, then the solid features built on it; lengths are millimeters unless a unit is written):

FEATURE [Sketcher::SketchObject] Sketch  label="profileDeBase"
  FullyConstrained = true
  MapMode = 5
  Placement = pos=(0,0,0) rot=(0.57735,0.57735,0.57735;2.0944rad)
  Support = -> [YZ_Plane001]
  expr: Constraints[10] = <<sp>>.petitRetour
  expr: Constraints[11] = <<sp>>.angleFacePetitRetour
  expr: Constraints[12] = <<sp>>.Face
  expr: Constraints[13] = <<sp>>.angleFaceRetourHaut
  expr: Constraints[8] = <<sp>>.Base
  expr: Constraints[9] = <<sp>>.anglePetitRetourBase
  sketch-geometry (5):
    g0: LineSegment StartX=0 StartY=0 StartZ=0 EndX=-65 EndY=0 EndZ=0
    g1: LineSegment StartX=-65 StartY=0 StartZ=0 EndX=-79.1421 EndY=14.1421 EndZ=0
    g2: LineSegment StartX=-79.1421 StartY=14.1421 StartZ=0 EndX=-22.5736 EndY=70.7107 EndZ=0
    g3: LineSegment StartX=-22.5736 StartY=70.7107 StartZ=0 EndX=0 EndY=48.1371 EndZ=0
    g4: LineSegment StartX=0 StartY=48.1371 StartZ=0 EndX=0 EndY=0 EndZ=0
  constraints (14):
    c: Coincident(g-1,g0)
    c: Horizontal(g0)
    c: Coincident(g0,g1)
    c: Coincident(g1,g2)
    c: Coincident(g2,g3)
    c: PointOnObject(g3,g-2)
    c: Coincident(g3,g4)
    c: Coincident(g4,g0)
    c: DistanceX(g0,g0) = 65
    c: Angle(g0,g1) = 2.35619
    c: Distance(g1) = 20
    c: Angle(g1,g2) = 1.5708
    c: Distance(g2) = 80
    c: Angle(g2,g3) = 1.5708
FEATURE [PartDesign::Pad] Pad
  AllowMultiFace = false
  Direction = (1,-2e-16,3e-16)
  Length = 50
  Length2 = 100
  Placement = pos=(0,0,0) rot=(0.57735,0.57735,0.57735;2.0944rad)
  Profile = -> Sketch
  Reversed = true
  Type = 0
  expr: Length = <<sp>>.largeurModuleBase
FEATURE [PartDesign::Plane] DatumPlane
  AttachmentOffset = pos=(71,0,0) rot=(0,-1,0;0.785398rad)
  Length = 98.6412
  MapMode = 5
  Placement = pos=(-1.18e-14,1.18e-14,71) rot=(0.678598,0.678598,0.281085;3.68962rad)
  ResizeMode = 0
  Support = -> [Pad]
  Width = 63.0813
FEATURE [PartDesign::Body] Body  label="Base"
  Group = -> [Sketch,Pad,DatumPlane]
  Origin = -> Origin001
  Tip = -> Pad
COMPONENT P3 — recipe-attached ("tigeLaiton001", modeled in this document).
Construction recipe (the document's own serialized feature program — sketch geometry with constraints, then the solid features built on it; lengths are millimeters unless a unit is written):

FEATURE [PartDesign::Plane] DatumPlane012  label="planBaseTige"
  AttachmentOffset = pos=(0,0,-5.18) rot=(0,0,1;0rad)
  Length = 60
  MapMode = 5
  Placement = pos=(-5.18,1.2e-15,-1.2e-15) rot=(0.57735,0.57735,0.57735;2.0944rad)
  ResizeMode = 0
  Support = -> [YZ_Plane012]
  Width = 60
  expr: .AttachmentOffset.Base.z = -<<tige>>.planBaseTigeposX
FEATURE [Sketcher::SketchObject] Sketch032  label="sk_tiges"
  FullyConstrained = true
  MapMode = 5
  Placement = pos=(-5.18,1.2e-15,-1.2e-15) rot=(0.57735,0.57735,0.57735;2.0944rad)
  Support = -> [DatumPlane012]
  expr: Constraints[0] = <<tige>>.tigeDiam
  expr: Constraints[1] = <<tige>>.tigePosY
  expr: Constraints[2] = <<tige>>.tigePosX
  sketch-geometry (1):
    g0: Circle CenterX=-14 CenterY=14.3 CenterZ=0 NormalX=0 NormalY=0 NormalZ=1 AngleXU=0 Radius=1.25
  constraints (3):
    c: Diameter(g0) = 2.5
    c: DistanceY(g-1,g0) = 14.3
    c: DistanceX(g0,g-1) = 14
FEATURE [PartDesign::Pad] Pad017  label="tigeBasse"
  AllowMultiFace = false
  Direction = (1,-1e-16,1e-16)
  Length = 33.62
  Length2 = 100
  Placement = pos=(-5.18,1.2e-15,-1.2e-15) rot=(0.57735,0.57735,0.57735;2.0944rad)
  Profile = -> Sketch032
  Reversed = true
  Type = 0
  expr: Length = <<tige>>.tigeLong
FEATURE [PartDesign::Body] Body007  label="tigeLaiton"
  Group = -> [DatumPlane012,Sketch032,Pad017]
  Origin = -> Origin016
  Tip = -> Pad017
FEATURE [PartDesign::Plane] DatumPlane013  label="planTige2"
  AttachmentOffset = pos=(0,0,-5.18) rot=(0,0,1;0rad)
  Length = 60
  MapMode = 5
  Placement = pos=(-5.18,1.2e-15,-1.2e-15) rot=(0.57735,0.57735,0.57735;2.0944rad)
  ResizeMode = 0
  Support = -> [YZ_Plane014]
  Width = 60
  expr: .AttachmentOffset.Base.z = -<<tige>>.planBaseTigeposX
FEATURE [Sketcher::SketchObject] Sketch033  label="sk_tige2"
  FullyConstrained = true
  MapMode = 5
  Placement = pos=(-5.18,1.2e-15,-1.2e-15) rot=(0.57735,0.57735,0.57735;2.0944rad)
  Support = -> [DatumPlane013]
  expr: Constraints[0] = <<tige>>.tigeDiam
  expr: Constraints[1] = <<tige>>.tigePosX
  expr: Constraints[2] = <<tige>>.tigePosY + <<tige>>.xtEcartBroches
  sketch-geometry (1):
    g0: Circle CenterX=-14 CenterY=21.86 CenterZ=0 NormalX=0 NormalY=0 NormalZ=1 AngleXU=0 Radius=1.25
  constraints (3):
    c: Diameter(g0) = 2.5
    c: DistanceX(g0,g-1) = 14
    c: DistanceY(g-1,g0) = 21.86
FEATURE [PartDesign::Pad] Pad018
  AllowMultiFace = false
  Direction = (1,-1e-16,1e-16)
  Length = 33.62
  Length2 = 100
  Placement = pos=(-5.18,1.2e-15,-1.2e-15) rot=(0.57735,0.57735,0.57735;2.0944rad)
  Profile = -> Sketch033
  Reversed = true
  Type = 0
  expr: Length = <<tige>>.tigeLong
FEATURE [PartDesign::Body] Body008  label="tige2"
  Group = -> [DatumPlane013,Sketch033,Pad018]
  Origin = -> Origin018
  Tip = -> Pad018
COMPONENT P4 — geometry summary ("xtVisInsertFix"; no construction recipe available for this part):
  bounding box: 20.2 x 17.7 x 16.6 mm
  tessellated surface: 23,208 triangles
  volume: 1306 mm^3 (22% of its bounding box)
COMPONENT P5 — geometry summary ("xtVisInertMob"; no construction recipe available for this part):
  bounding box: 20.5 x 17.8 x 16.5 mm
  tessellated surface: 35,220 triangles
  volume: 1060 mm^3 (18% of its bounding box)
COMPONENT P6 — recipe-attached ("visInsertFavFix", modeled in this document).
Construction recipe (the document's own serialized feature program — sketch geometry with constraints, then the solid features built on it; lengths are millimeters unless a unit is written):

FEATURE [Sketcher::SketchObject] Sketch034  label="Sketch"
  FullyConstrained = false
  MapMode = 5
  Support = -> [XY_Plane015]
  sketch-geometry (1):
    g0: Circle CenterX=0 CenterY=0 CenterZ=0 NormalX=0 NormalY=0 NormalZ=1 AngleXU=0 Radius=2.75
  constraints (2):
    c: Coincident(g0,g-1)
    c: Diameter(g0) = 5.5
FEATURE [PartDesign::Pad] Pad019  label="tete"
  AllowMultiFace = false
  Direction = (1,1,1)
  Length = 3
  Length2 = 100
  Profile = -> Sketch034
  Type = 0
FEATURE [Sketcher::SketchObject] Sketch001
  FullyConstrained = false
  MapMode = 5
  Placement = pos=(0,0,0) rot=(1,0,0;3.14159rad)
  Support = -> [Pad019]
  sketch-geometry (1):
    g0: Circle CenterX=0 CenterY=0 CenterZ=0 NormalX=0 NormalY=0 NormalZ=1 AngleXU=0 Radius=1.5
  constraints (2):
    c: Coincident(g0,g-1)
    c: Diameter(g0) = 3
FEATURE [PartDesign::Pad] Pad020  label="corps"
  AllowMultiFace = false
  BaseFeature = -> Pad019
  Direction = (1,1,1)
  Length = 6
  Length2 = 100
  Profile = -> Sketch001
  Type = 0
FEATURE [PartDesign::Plane] DatumPlane014
  AttachmentOffset = pos=(0,0,3) rot=(0,0,1;0rad)
  Length = 60
  MapMode = 5
  Placement = pos=(0,0,3) rot=(0,0,1;0rad)
  ResizeMode = 0
  Support = -> [XY_Plane015]
  Width = 60
FEATURE [Sketcher::SketchObject] Sketch035  label="Sketch002"
  FullyConstrained = false
  MapMode = 5
  Placement = pos=(0,0,3) rot=(0,0,1;0rad)
  Support = -> [DatumPlane014]
  sketch-geometry (7):
    g0: LineSegment StartX=0.721688 StartY=-1.25 StartZ=0 EndX=1.44338 EndY=1.0119e-12 EndZ=0
    g1: LineSegment StartX=1.44338 StartY=1.0119e-12 StartZ=0 EndX=0.721688 EndY=1.25 EndZ=0
    g2: LineSegment StartX=0.721688 StartY=1.25 StartZ=0 EndX=-0.721688 EndY=1.25 EndZ=0
    g3: LineSegment StartX=-0.721688 StartY=1.25 StartZ=0 EndX=-1.44338 EndY=8.689e-13 EndZ=0
    g4: LineSegment StartX=-1.44338 StartY=8.689e-13 StartZ=0 EndX=-0.721688 EndY=-1.25 EndZ=0
    g5: LineSegment StartX=-0.721688 StartY=-1.25 StartZ=0 EndX=0.721688 EndY=-1.25 EndZ=0
    g6: Circle CenterX=0 CenterY=0 CenterZ=0 NormalX=0 NormalY=0 NormalZ=1 AngleXU=0 Radius=1.44338
  constraints (16):
    c: Coincident(g0,g1)
    c: Coincident(g1,g2)
    c: Coincident(g2,g3)
    c: Coincident(g3,g4)
    c: Coincident(g4,g5)
    c: Coincident(g5,g0)
    c: Equal(g0, g1-g5) x5
    c: PointOnObject(g0,g6)
    c: PointOnObject(g1,g6)
    c: PointOnObject(g2,g6)
    c: PointOnObject(g3,g6)
    c: PointOnObject(g4,g6)
    c: PointOnObject(g5,g6)
    c: Coincident(g6,g-1)
    c: Horizontal(g2)
    c: DistanceY(g0,g1) = 2.5
FEATURE [PartDesign::Pocket] Pocket016  label="emprunte"
  AllowMultiFace = false
  BaseFeature = -> Pad020
  Direction = (1,1,1)
  Length = 4
  Length2 = 100
  Profile = -> Sketch035
  Type = 0
FEATURE [PartDesign::Body] Body009  label="visTHCM3x6_FAV001"
  Group = -> [Sketch034,Pad019,Sketch001,Pad020,DatumPlane014,Sketch035,Pocket016]
  Origin = -> Origin019
  Placement = pos=(-6.5,-61.8718,6.01041) rot=(1,0,0;3.92699rad)
  Tip = -> Pocket016
COMPONENT P7 — recipe-attached ("visInserFavMob", modeled in this document).
Construction recipe (the document's own serialized feature program — sketch geometry with constraints, then the solid features built on it; lengths are millimeters unless a unit is written):

FEATURE [Sketcher::SketchObject] Sketch036
  FullyConstrained = false
  MapMode = 5
  Support = -> [XY_Plane016]
  sketch-geometry (1):
    g0: Circle CenterX=0 CenterY=0 CenterZ=0 NormalX=0 NormalY=0 NormalZ=1 AngleXU=0 Radius=2.75
  constraints (2):
    c: Coincident(g0,g-1)
    c: Diameter(g0) = 5.5
FEATURE [PartDesign::Pad] Pad021  label="tete001"
  AllowMultiFace = false
  Direction = (1,1,1)
  Length = 3
  Length2 = 100
  Profile = -> Sketch036
  Type = 0
FEATURE [Sketcher::SketchObject] Sketch037
  FullyConstrained = false
  MapMode = 5
  Placement = pos=(0,0,0) rot=(1,0,0;3.14159rad)
  Support = -> [Pad021]
  sketch-geometry (1):
    g0: Circle CenterX=0 CenterY=0 CenterZ=0 NormalX=0 NormalY=0 NormalZ=1 AngleXU=0 Radius=1.5
  constraints (2):
    c: Coincident(g0,g-1)
    c: Diameter(g0) = 3
FEATURE [PartDesign::Pad] Pad022  label="corps001"
  AllowMultiFace = false
  BaseFeature = -> Pad021
  Direction = (1,1,1)
  Length = 6
  Length2 = 100
  Profile = -> Sketch037
  Type = 0
FEATURE [PartDesign::Plane] DatumPlane015
  AttachmentOffset = pos=(0,0,3) rot=(0,0,1;0rad)
  Length = 60
  MapMode = 5
  Placement = pos=(0,0,3) rot=(0,0,1;0rad)
  ResizeMode = 0
  Support = -> [XY_Plane016]
  Width = 60
FEATURE [Sketcher::SketchObject] Sketch038
  FullyConstrained = false
  MapMode = 5
  Placement = pos=(0,0,3) rot=(0,0,1;0rad)
  Support = -> [DatumPlane015]
  sketch-geometry (7):
    g0: LineSegment StartX=0.721688 StartY=-1.25 StartZ=0 EndX=1.44338 EndY=1.0119e-12 EndZ=0
    g1: LineSegment StartX=1.44338 StartY=1.0119e-12 StartZ=0 EndX=0.721688 EndY=1.25 EndZ=0
    g2: LineSegment StartX=0.721688 StartY=1.25 StartZ=0 EndX=-0.721688 EndY=1.25 EndZ=0
    g3: LineSegment StartX=-0.721688 StartY=1.25 StartZ=0 EndX=-1.44338 EndY=8.689e-13 EndZ=0
    g4: LineSegment StartX=-1.44338 StartY=8.689e-13 StartZ=0 EndX=-0.721688 EndY=-1.25 EndZ=0
    g5: LineSegment StartX=-0.721688 StartY=-1.25 StartZ=0 EndX=0.721688 EndY=-1.25 EndZ=0
    g6: Circle CenterX=0 CenterY=0 CenterZ=0 NormalX=0 NormalY=0 NormalZ=1 AngleXU=0 Radius=1.44338
  constraints (16):
    c: Coincident(g0,g1)
    c: Coincident(g1,g2)
    c: Coincident(g2,g3)
    c: Coincident(g3,g4)
    c: Coincident(g4,g5)
    c: Coincident(g5,g0)
    c: Equal(g0, g1-g5) x5
    c: PointOnObject(g0,g6)
    c: PointOnObject(g1,g6)
    c: PointOnObject(g2,g6)
    c: PointOnObject(g3,g6)
    c: PointOnObject(g4,g6)
    c: PointOnObject(g5,g6)
    c: Coincident(g6,g-1)
    c: Horizontal(g2)
    c: DistanceY(g0,g1) = 2.5
FEATURE [PartDesign::Pocket] Pocket017  label="emprunte001"
  AllowMultiFace = false
  BaseFeature = -> Pad022
  Direction = (1,1,1)
  Length = 4
  Length2 = 100
  Profile = -> Sketch038
  Type = 0
FEATURE [PartDesign::Body] Body010  label="visTHCM3x6_FAV002"
  Group = -> [Sketch036,Pad021,Sketch037,Pad022,DatumPlane015,Sketch038,Pocket017]
  Origin = -> Origin020
  Placement = pos=(-28.5,-61.8718,6.01041) rot=(1,0,0;3.92699rad)
  Tip = -> Pocket017
PROVENANCE & LICENSES
A FreeCAD (.FCStd) document from a public repository crawl; recipes are the document's own serialized feature recipes (and, for linked parts, companion documents' recipes).
License: as declared in the source repository (recorded in the dataset sidecar).
